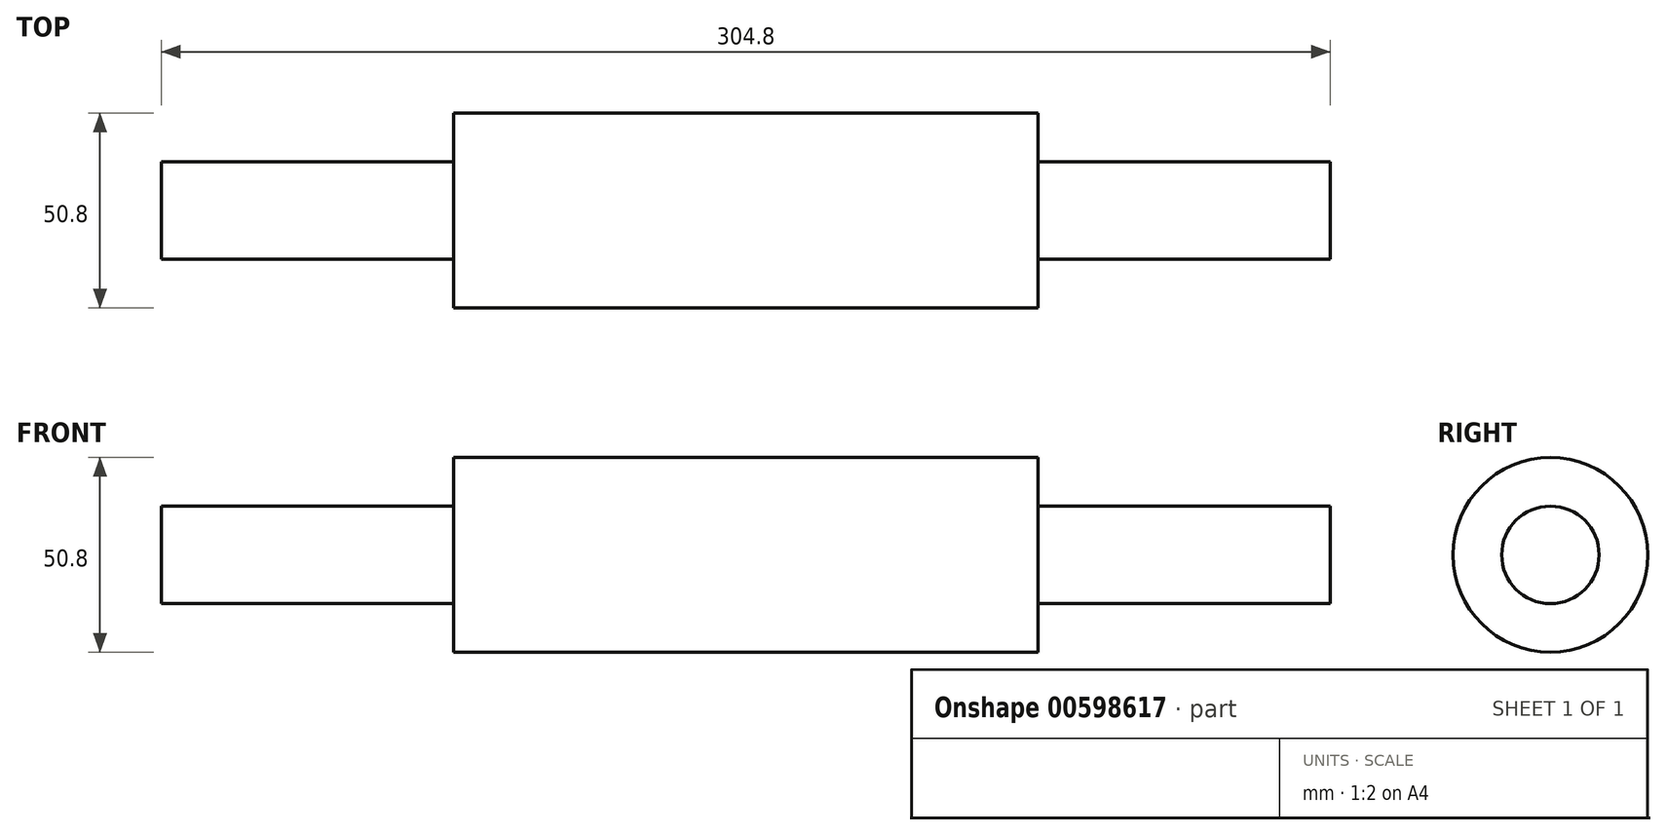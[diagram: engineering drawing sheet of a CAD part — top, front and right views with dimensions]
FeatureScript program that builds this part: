
annotation { "Feature Type Name" : "Feature", "Feature Type Description" : "" }
export const myFeature = defineFeature(function(context is Context, id is Id, definition is map)
    precondition{}
    {
        {
            var Q0;
            Q0=qCreatedBy(makeId("Right.planeOp"),FACE);
            var sketch = newSketch(context, id + "F0", { "sketchPlane" : qUnion([Q0])});
            skCircle(sketch, "E0", {"center": v(0, 0) * mm, "radius": 25.4 * mm});
            skSolve(sketch);
        }
        {
            var Q0;
            Q0=makeQuery(id+"F0.imprint","IMPRINT",FACE,{"disambiguationData":[TD([[makeQuery(id+"F0.imprint","IMPRINT",EDGE,{"derivedFrom":sQuery(id+"F0.wireOp",EDGE,"E0")}),1.0]])]});
            extrude(context, id + "F1", {"entities" : qUnion([Q0]), "depth" : 152.4 * mm, "offsetDistance" : 25.4 * mm});
        }
        {
            var Q0;
            Q0=makeQuery(id+"F1.opExtrude","CAP_FACE",FACE,{"disambiguationData":[OSD([sQuery(id+"F0.wireOp",EDGE,"E0")])],"isStart":false});
            var sketch = newSketch(context, id + "F2", { "sketchPlane" : qUnion([Q0])});
            skCircle(sketch, "E1", {"center": v(0, 0) * mm, "radius": 12.7 * mm});
            skSolve(sketch);
        }
        {
            var Q0;
            Q0=makeQuery(id+"F2.imprint","IMPRINT",FACE,{"disambiguationData":[TD([[makeQuery(id+"F2.imprint","IMPRINT",EDGE,{"derivedFrom":sQuery(id+"F2.wireOp",EDGE,"E1")}),1.0]])]});
            extrude(context, id + "F3", {"entities" : qUnion([Q0]), "operationType" : NewBodyOperationType.ADD, "depth" : 76.2 * mm, "offsetDistance" : 25.4 * mm});
        }
        {
            var Q0;
            Q0=makeQuery(id+"F1.opExtrude","CAP_FACE",FACE,{"disambiguationData":[OSD([sQuery(id+"F0.wireOp",EDGE,"E0")])],"isStart":true});
            var sketch = newSketch(context, id + "F4", { "sketchPlane" : qUnion([Q0])});
            skCircle(sketch, "E2", {"center": v(0, 0) * mm, "radius": 12.7 * mm});
            skSolve(sketch);
        }
        {
            var Q0;
            Q0=makeQuery(id+"F4.imprint","IMPRINT",FACE,{"disambiguationData":[TD([[makeQuery(id+"F4.imprint","IMPRINT",EDGE,{"derivedFrom":sQuery(id+"F4.wireOp",EDGE,"E2")}),1.0]])]});
            extrude(context, id + "F5", {"entities" : qUnion([Q0]), "operationType" : NewBodyOperationType.ADD, "depth" : 76.2 * mm, "offsetDistance" : 25.4 * mm});
        }
    });
